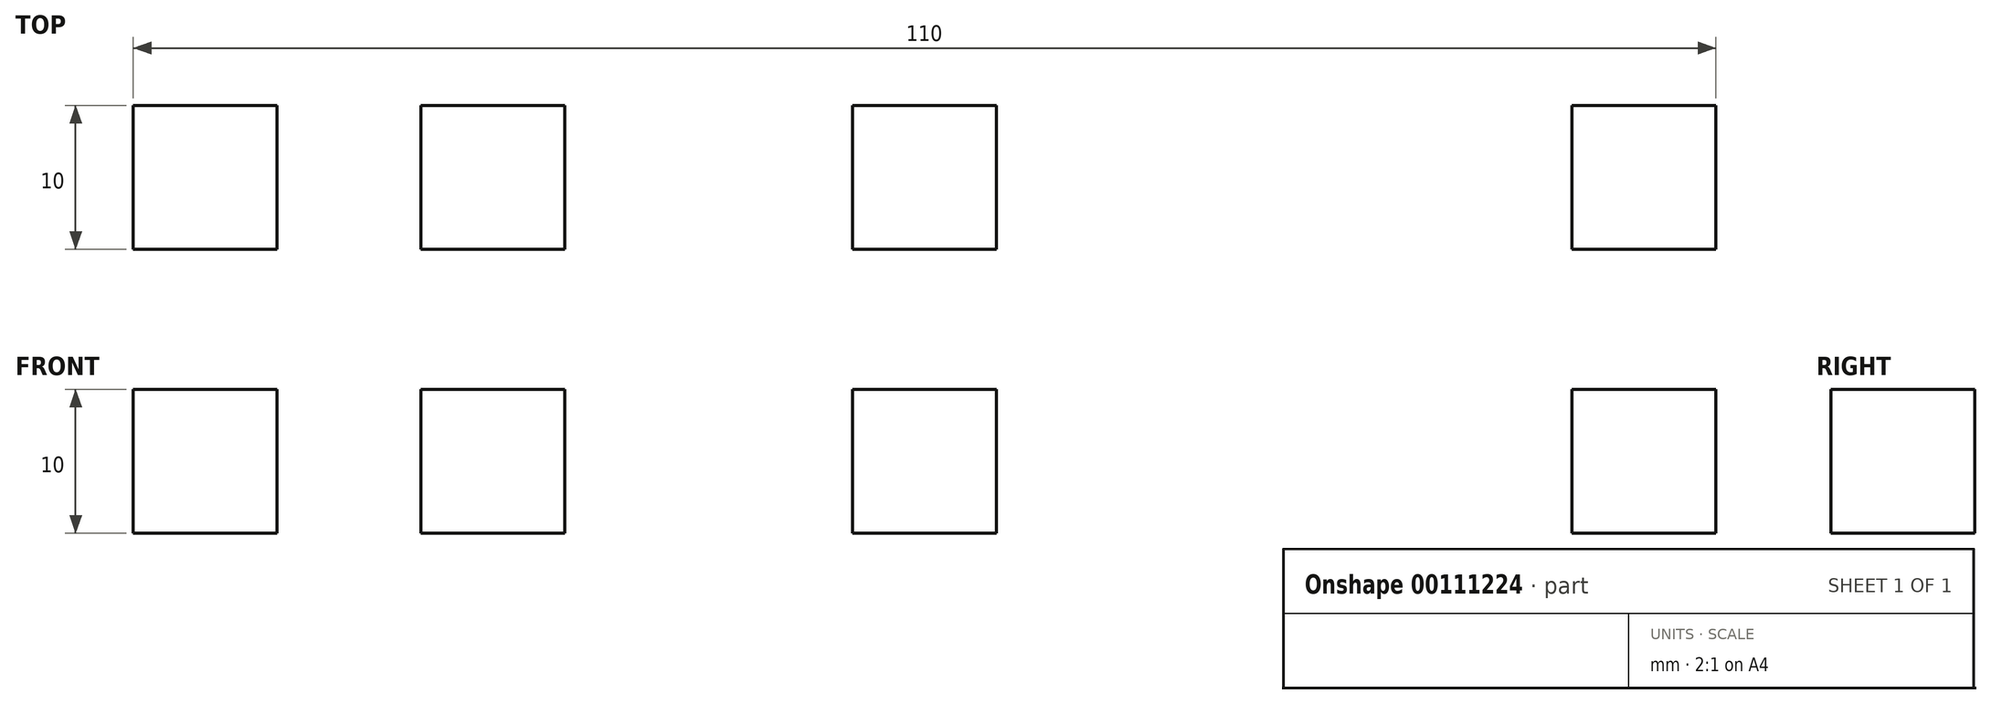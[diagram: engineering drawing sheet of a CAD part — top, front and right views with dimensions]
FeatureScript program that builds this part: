
annotation { "Feature Type Name" : "Feature", "Feature Type Description" : "" }
export const myFeature = defineFeature(function(context is Context, id is Id, definition is map)
    precondition{}
    {
        {
            var Q0;
            Q0=qCreatedBy(makeId("Top.planeOp"),FACE);
            var sketch = newSketch(context, id + "F0", { "sketchPlane" : qUnion([Q0])});
            skLineSegment(sketch, "E0.bottom", {"start": v(-48.22, 0) * mm, "end": v(-38.22, 0) * mm});
            skLineSegment(sketch, "E0.top", {"start": v(-48.22, -10) * mm, "end": v(-38.22, -10) * mm});
            skLineSegment(sketch, "E0.left", {"start": v(-48.22, 0) * mm, "end": v(-48.22, -10) * mm});
            skLineSegment(sketch, "E0.right", {"start": v(-38.22, 0) * mm, "end": v(-38.22, -10) * mm});
            skLineSegment(sketch, "E1.bottom", {"start": v(-28.22, 0) * mm, "end": v(-18.22, 0) * mm});
            skLineSegment(sketch, "E1.top", {"start": v(-28.22, -10) * mm, "end": v(-18.22, -10) * mm});
            skLineSegment(sketch, "E1.left", {"start": v(-28.22, 0) * mm, "end": v(-28.22, -10) * mm});
            skLineSegment(sketch, "E1.right", {"start": v(-18.22, 0) * mm, "end": v(-18.22, -10) * mm});
            skLineSegment(sketch, "E2.bottom", {"start": v(1.78, 0) * mm, "end": v(11.78, 0) * mm});
            skLineSegment(sketch, "E2.top", {"start": v(1.78, -10) * mm, "end": v(11.78, -10) * mm});
            skLineSegment(sketch, "E2.left", {"start": v(1.78, 0) * mm, "end": v(1.78, -10) * mm});
            skLineSegment(sketch, "E2.right", {"start": v(11.78, 0) * mm, "end": v(11.78, -10) * mm});
            skLineSegment(sketch, "E3.bottom", {"start": v(51.78, 0) * mm, "end": v(61.78, 0) * mm});
            skLineSegment(sketch, "E3.top", {"start": v(51.78, -10) * mm, "end": v(61.78, -10) * mm});
            skLineSegment(sketch, "E3.left", {"start": v(51.78, 0) * mm, "end": v(51.78, -10) * mm});
            skLineSegment(sketch, "E3.right", {"start": v(61.78, 0) * mm, "end": v(61.78, -10) * mm});
            skSolve(sketch);
        }
        {
            var Q0;
            Q0 = qSketchRegion(id + "F0", true);
            extrude(context, id + "F1", {"entities" : qUnion([Q0]), "depth" : 10 * mm});
        }
    });
